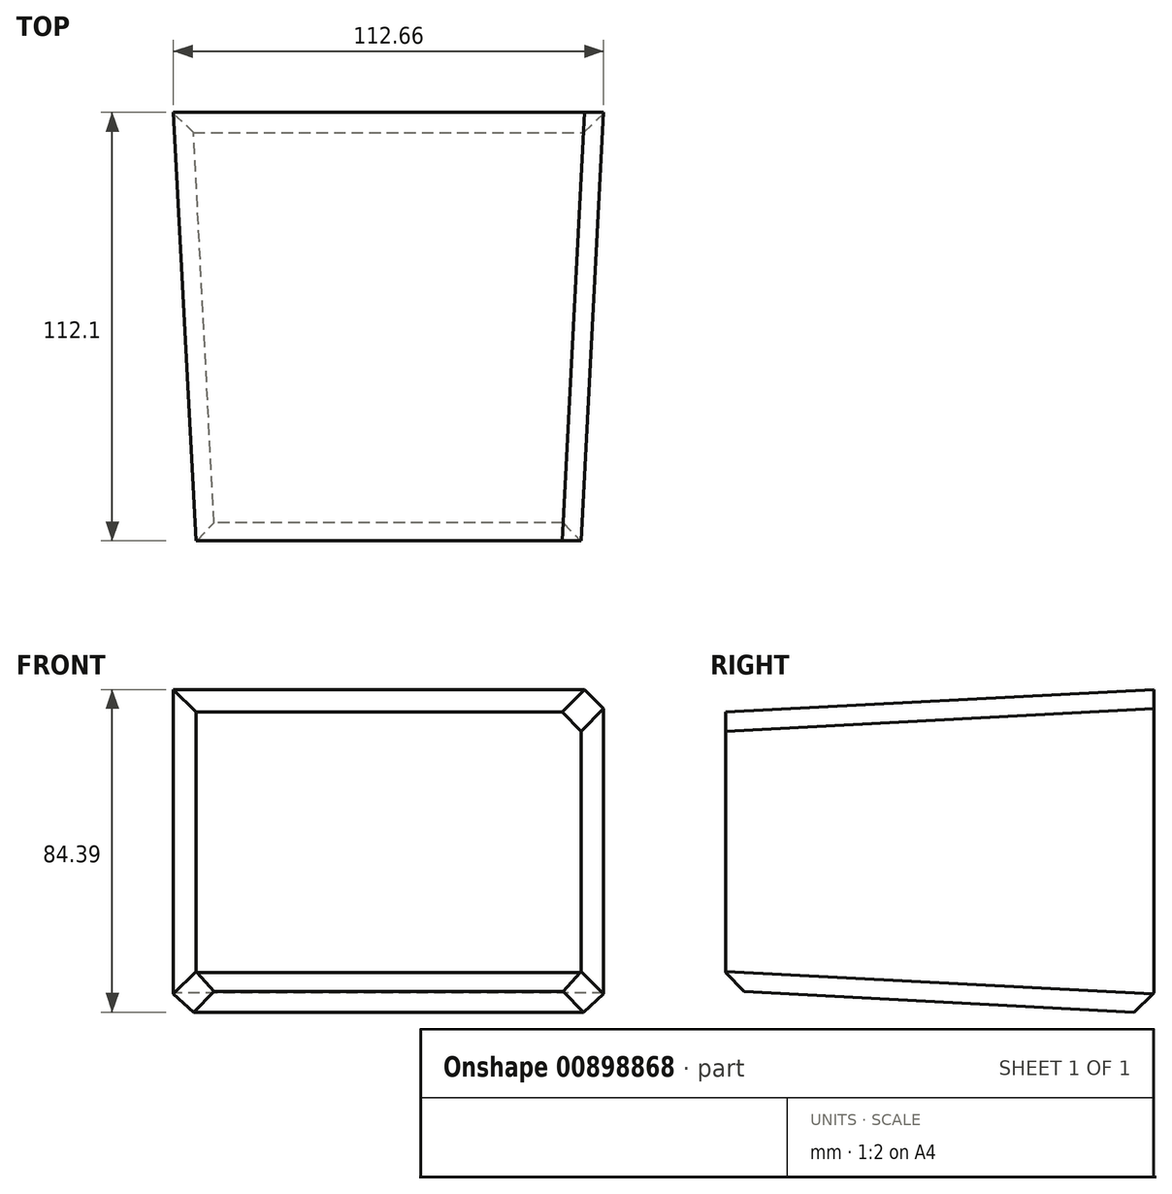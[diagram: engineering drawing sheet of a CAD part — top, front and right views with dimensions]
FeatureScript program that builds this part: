
annotation { "Feature Type Name" : "Feature", "Feature Type Description" : "" }
export const myFeature = defineFeature(function(context is Context, id is Id, definition is map)
    precondition{}
    {
        {
            var Q0;
            Q0=qCreatedBy(makeId("Front.planeOp"),FACE);
            var sketch = newSketch(context, id + "F0", { "sketchPlane" : qUnion([Q0])});
            skLineSegment(sketch, "E0.bottom", {"start": v(56.33, 42.33) * mm, "end": v(-56.33, 42.33) * mm});
            skLineSegment(sketch, "E0.top", {"start": v(56.33, -42.33) * mm, "end": v(-56.33, -42.33) * mm});
            skLineSegment(sketch, "E0.left", {"start": v(56.33, 42.33) * mm, "end": v(56.33, -42.33) * mm});
            skLineSegment(sketch, "E0.right", {"start": v(-56.33, 42.33) * mm, "end": v(-56.33, -42.33) * mm});
            skPoint(sketch, "E0.middle", {"position": v(0, 0) * mm});
            skSolve(sketch);
        }
        {
            var Q0;
            Q0 = qSketchRegion(id + "F0", true);
            var Q1;
            Q1=makeQuery(id+"F0.imprint","IMPRINT",FACE,{"disambiguationData":[TD([[makeQuery(id+"F0.imprint","IMPRINT",EDGE,{"derivedFrom":sQuery(id+"F0.wireOp",EDGE,"E0.bottom")}),1.0]])]});
            extrude(context, id + "F1", {"entities" : qUnion([Q0, Q1]), "depth" : 112.1 * mm, "offsetDistance" : 25 * mm, "hasDraft" : true, "draftAngle" : 3 * degree, "draftPullDirection" : true});
        }
        {
            var Q0;
            Q0=makeQuery(id+"F1.opExtrude","SWEPT_EDGE",EDGE,{"disambiguationData":[OSD([sQuery(id+"F0.wireOp",EDGE,"E0.bottom"),sQuery(id+"F0.wireOp",EDGE,"E0.left")])]});
            var Q1;
            Q1=makeQuery(id+"F1.opExtrude","SWEPT_FACE",FACE,{"disambiguationData":[OSD([sQuery(id+"F0.wireOp",EDGE,"E0.top")])]});
            chamfer(context, id + "F2", {"entities" : qUnion([Q0, Q1]), "width" : 5 * mm, "tangentPropagation" : true});
        }
    });
